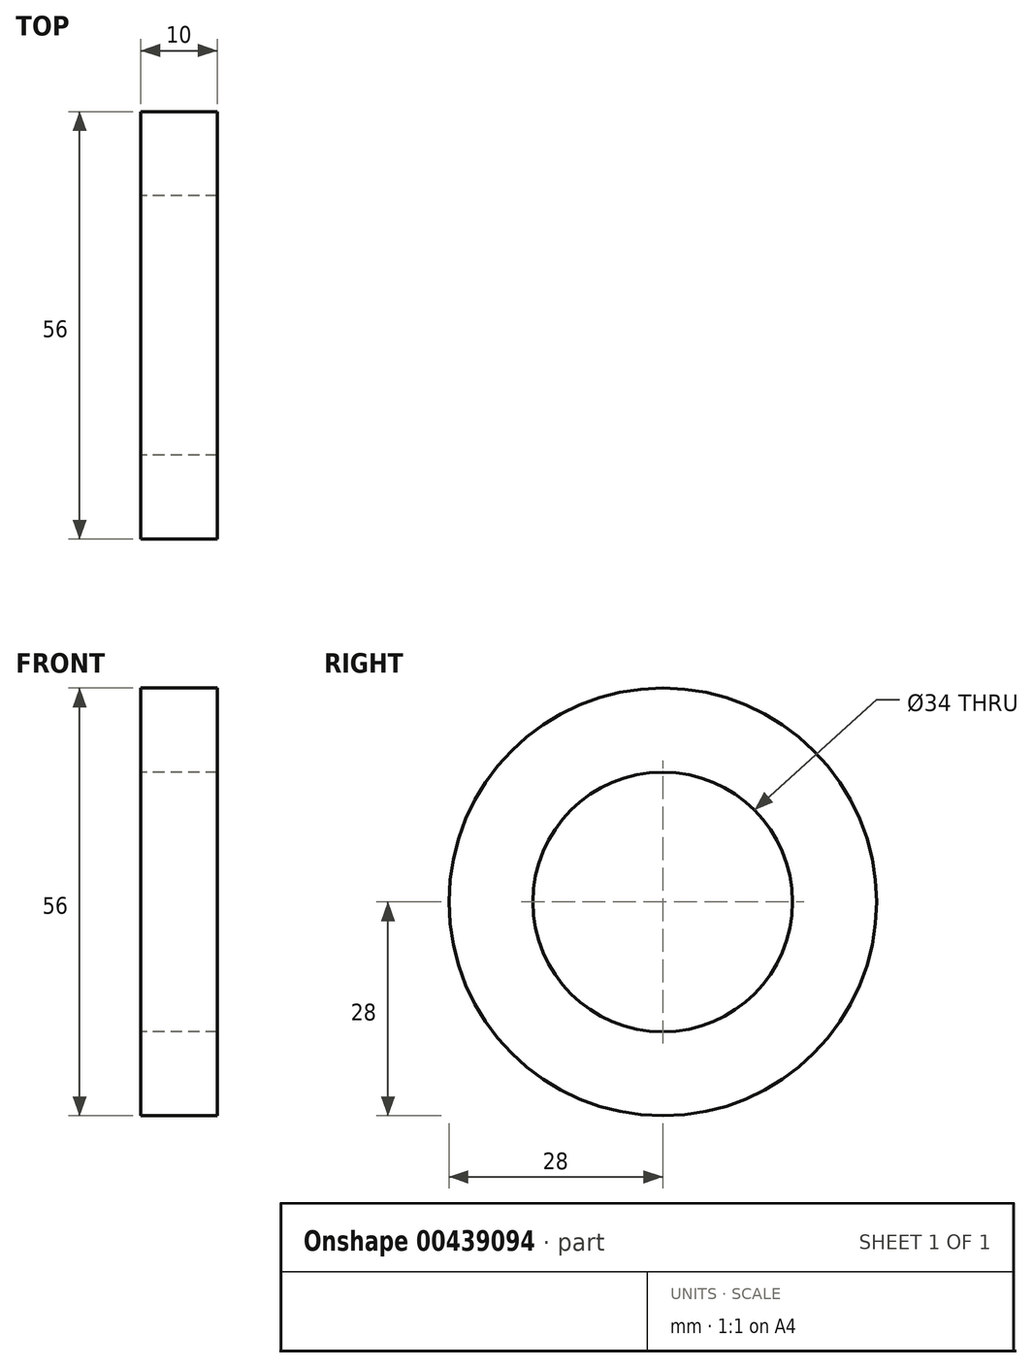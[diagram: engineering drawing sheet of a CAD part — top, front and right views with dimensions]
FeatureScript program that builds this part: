
annotation { "Feature Type Name" : "Feature", "Feature Type Description" : "" }
export const myFeature = defineFeature(function(context is Context, id is Id, definition is map)
    precondition{}
    {
        {
            var Q0;
            Q0=qCreatedBy(makeId("Right.planeOp"),FACE);
            var sketch = newSketch(context, id + "F0", { "sketchPlane" : qUnion([Q0])});
            skCircle(sketch, "E0", {"center": v(0, 0) * mm, "radius": 28 * mm});
            skCircle(sketch, "E1", {"center": v(0, 0) * mm, "radius": 17 * mm});
            skSolve(sketch);
        }
        {
            var Q0;
            Q0=qSketchRegion(id+"F0",true);
            extrude(context, id + "F1", {"entities" : qUnion([Q0]), "depth" : 10 * mm});
        }
    });
